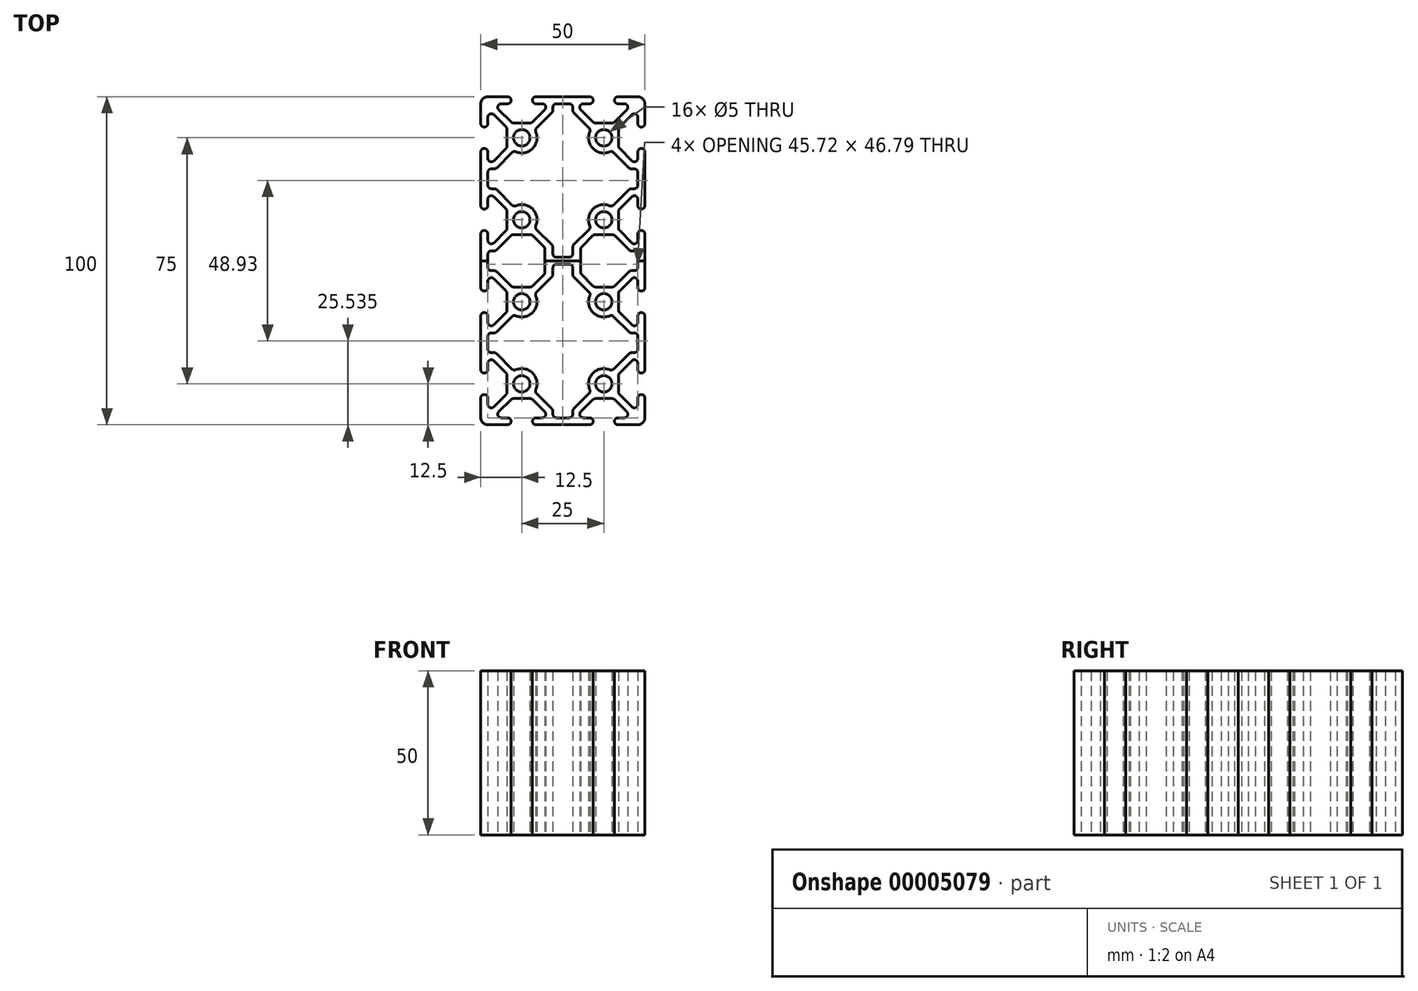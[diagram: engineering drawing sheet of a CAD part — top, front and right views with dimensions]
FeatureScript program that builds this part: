
annotation { "Feature Type Name" : "Feature", "Feature Type Description" : "" }
export const myFeature = defineFeature(function(context is Context, id is Id, definition is map)
    precondition{}
    {
        {
            var Q0;
            Q0=qCreatedBy(makeId("Top.planeOp"),FACE);
            var sketch = newSketch(context, id + "F0", { "sketchPlane" : qUnion([Q0])});
            skLineSegment(sketch, "E0", {"start": v(-12.5, 12.5) * mm, "end": v(-25, 25) * mm, "construction": true});
            skLineSegment(sketch, "E1", {"start": v(-25, 22.86) * mm, "end": v(-25, 16.82) * mm});
            skLineSegment(sketch, "E2", {"start": v(-22.86, 25) * mm, "end": v(-16.82, 25) * mm});
            skLineSegment(sketch, "E3", {"start": v(-16.82, 22.86) * mm, "end": v(-18.76, 22.86) * mm});
            skLineSegment(sketch, "E4", {"start": v(-22.86, 18.76) * mm, "end": v(-22.86, 16.82) * mm});
            skArc(sketch, "E5", {"start": v(-16.82, 25) * mm, "mid": v(-15.75, 23.93) * mm, "end": v(-16.82, 22.86) * mm});
            skArc(sketch, "E6", {"start": v(-22.86, 16.82) * mm, "mid": v(-23.93, 15.75) * mm, "end": v(-25, 16.82) * mm});
            skLineSegment(sketch, "E7", {"start": v(-19.52, 21.03) * mm, "end": v(-15.81, 17.32) * mm});
            skPoint(sketch, "E8.visualSharp", {"position": v(-25, 25) * mm});
            skLineSegment(sketch, "E8.filletArc", {"start": v(-25, 25) * mm, "end": v(-25, 25) * mm});
            skArc(sketch, "E9.filletArc", {"start": v(-21.03, 19.52) * mm, "mid": v(-22.2, 19.75) * mm, "end": v(-22.86, 18.76) * mm});
            skPoint(sketch, "E10.visualSharp", {"position": v(-21.35, 22.86) * mm});
            skArc(sketch, "E10.filletArc", {"start": v(-18.76, 22.86) * mm, "mid": v(-19.75, 22.2) * mm, "end": v(-19.52, 21.03) * mm});
            skArc(sketch, "E11.filletArc", {"start": v(-15.81, 17.32) * mm, "mid": v(-15.46, 17.1) * mm, "end": v(-15.05, 17.01) * mm});
            skCircle(sketch, "E12", {"center": v(-12.5, 12.5) * mm, "radius": 2.5 * mm});
            skLineSegment(sketch, "E13", {"start": v(0, 0) * mm, "end": v(0, 12.39) * mm, "construction": true});
            skCircle(sketch, "E14.0.MirrorC", {"center": v(12.5, 12.5) * mm, "radius": 2.5 * mm});
            skLineSegment(sketch, "E15", {"start": v(-12.5, 0) * mm, "end": v(-12.5, 12.5) * mm, "construction": true});
            skArc(sketch, "E16.0.MirrorCS", {"start": v(-9.19, 17.32) * mm, "mid": v(-9.54, 17.1) * mm, "end": v(-9.95, 17.01) * mm});
            skLineSegment(sketch, "E16.1.MirrorCS", {"start": v(-8.18, 22.86) * mm, "end": v(-6.24, 22.86) * mm});
            skLineSegment(sketch, "E16.3.MirrorCS", {"start": v(-5.48, 21.03) * mm, "end": v(-9.19, 17.32) * mm});
            skArc(sketch, "E16.8.MirrorCS", {"start": v(-8.18, 25) * mm, "mid": v(-9.25, 23.93) * mm, "end": v(-8.18, 22.86) * mm});
            skArc(sketch, "E16.11.MirrorCS", {"start": v(-6.24, 22.86) * mm, "mid": v(-5.25, 22.2) * mm, "end": v(-5.48, 21.03) * mm});
            skLineSegment(sketch, "E16.17.MirrorCS", {"start": v(0, 25) * mm, "end": v(-8.18, 25) * mm});
            skLineSegment(sketch, "E17", {"start": v(-15.05, 17.01) * mm, "end": v(-9.95, 17.01) * mm});
            skArc(sketch, "E18.1.MirrorCS", {"start": v(15.81, 17.32) * mm, "mid": v(15.46, 17.1) * mm, "end": v(15.05, 17.01) * mm});
            skArc(sketch, "E18.2.MirrorCS", {"start": v(9.19, 17.32) * mm, "mid": v(9.54, 17.1) * mm, "end": v(9.95, 17.01) * mm});
            skArc(sketch, "E18.3.MirrorCS", {"start": v(22.86, 16.82) * mm, "mid": v(23.93, 15.75) * mm, "end": v(25, 16.82) * mm});
            skLineSegment(sketch, "E18.5.MirrorCS", {"start": v(8.18, 22.86) * mm, "end": v(6.24, 22.86) * mm});
            skLineSegment(sketch, "E18.6.MirrorCS", {"start": v(19.52, 21.03) * mm, "end": v(15.81, 17.32) * mm});
            skLineSegment(sketch, "E18.7.MirrorCS", {"start": v(5.48, 21.03) * mm, "end": v(9.19, 17.32) * mm});
            skLineSegment(sketch, "E18.8.MirrorCS", {"start": v(12.5, 12.5) * mm, "end": v(25, 25) * mm, "construction": true});
            skArc(sketch, "E18.10.MirrorCS", {"start": v(16.82, 25) * mm, "mid": v(15.75, 23.93) * mm, "end": v(16.82, 22.86) * mm});
            skLineSegment(sketch, "E18.11.MirrorCS", {"start": v(15.05, 17.01) * mm, "end": v(9.95, 17.01) * mm});
            skPoint(sketch, "E18.12.MirrorP", {"position": v(21.35, 22.86) * mm});
            skLineSegment(sketch, "E18.14.MirrorCS", {"start": v(22.86, 25) * mm, "end": v(16.82, 25) * mm});
            skArc(sketch, "E18.15.MirrorCS", {"start": v(21.03, 19.52) * mm, "mid": v(22.2, 19.75) * mm, "end": v(22.86, 18.76) * mm});
            skPoint(sketch, "E18.16.MirrorP", {"position": v(25, 25) * mm});
            skLineSegment(sketch, "E18.17.MirrorCS", {"start": v(25, 22.86) * mm, "end": v(25, 16.82) * mm});
            skArc(sketch, "E18.18.MirrorCS", {"start": v(6.24, 22.86) * mm, "mid": v(5.25, 22.2) * mm, "end": v(5.48, 21.03) * mm});
            skArc(sketch, "E18.20.MirrorCS", {"start": v(18.76, 22.86) * mm, "mid": v(19.75, 22.2) * mm, "end": v(19.52, 21.03) * mm});
            skArc(sketch, "E18.21.MirrorCS", {"start": v(8.18, 25) * mm, "mid": v(9.25, 23.93) * mm, "end": v(8.18, 22.86) * mm});
            skLineSegment(sketch, "E18.22.MirrorCS", {"start": v(25, 25) * mm, "end": v(25, 25) * mm});
            skLineSegment(sketch, "E18.24.MirrorCS", {"start": v(22.86, 18.76) * mm, "end": v(22.86, 16.82) * mm});
            skLineSegment(sketch, "E18.25.MirrorCS", {"start": v(16.82, 22.86) * mm, "end": v(18.76, 22.86) * mm});
            skLineSegment(sketch, "E18.26.MirrorCS", {"start": v(0, 25) * mm, "end": v(8.18, 25) * mm});
            skLineSegment(sketch, "E19", {"start": v(-21.03, 19.52) * mm, "end": v(-17.32, 15.81) * mm});
            skLineSegment(sketch, "E20", {"start": v(0, 0) * mm, "end": v(-29.45, 0) * mm, "construction": true});
            skLineSegment(sketch, "E21", {"start": v(-17, 15.05) * mm, "end": v(-17, 12.5) * mm});
            skLineSegment(sketch, "E22", {"start": v(-12.5, 12.5) * mm, "end": v(-25, 12.5) * mm, "construction": true});
            skLineSegment(sketch, "E23.0.MirrorCS", {"start": v(21.03, 19.52) * mm, "end": v(17.32, 15.81) * mm});
            skLineSegment(sketch, "E24.0.MirrorCS", {"start": v(17, 15.05) * mm, "end": v(17, 12.5) * mm});
            skLineSegment(sketch, "E25.0.MirrorCS", {"start": v(-17, 9.95) * mm, "end": v(-17, 12.5) * mm});
            skLineSegment(sketch, "E26.0.MirrorCS", {"start": v(-21.03, 5.48) * mm, "end": v(-17.32, 9.19) * mm});
            skArc(sketch, "E27.0.MirrorCS", {"start": v(-21.03, 5.48) * mm, "mid": v(-22.2, 5.25) * mm, "end": v(-22.86, 6.24) * mm});
            skLineSegment(sketch, "E28.0.MirrorCS", {"start": v(-22.86, 6.24) * mm, "end": v(-22.86, 8.18) * mm});
            skArc(sketch, "E29.0.MirrorCS", {"start": v(-22.86, 8.18) * mm, "mid": v(-23.93, 9.25) * mm, "end": v(-25, 8.18) * mm});
            skLineSegment(sketch, "E30.0.MirrorCS", {"start": v(-25, 0) * mm, "end": v(-25, 8.18) * mm});
            skLineSegment(sketch, "E31.0.MirrorCS", {"start": v(17, 9.95) * mm, "end": v(17, 12.5) * mm});
            skLineSegment(sketch, "E32.0.MirrorCS", {"start": v(21.03, 5.48) * mm, "end": v(17.32, 9.19) * mm});
            skArc(sketch, "E33.0.MirrorCS", {"start": v(21.03, 5.48) * mm, "mid": v(22.2, 5.25) * mm, "end": v(22.86, 6.24) * mm});
            skLineSegment(sketch, "E34.0.MirrorCS", {"start": v(22.86, 6.24) * mm, "end": v(22.86, 8.18) * mm});
            skArc(sketch, "E35.0.MirrorCS", {"start": v(22.86, 8.18) * mm, "mid": v(23.93, 9.25) * mm, "end": v(25, 8.18) * mm});
            skLineSegment(sketch, "E36.0.MirrorCS", {"start": v(25, 0) * mm, "end": v(25, 8.18) * mm});
            skPoint(sketch, "E37.visualSharp", {"position": v(-17, 15.5) * mm});
            skArc(sketch, "E37.filletArc", {"start": v(-17, 15.05) * mm, "mid": v(-17.1, 15.46) * mm, "end": v(-17.32, 15.81) * mm});
            skPoint(sketch, "E38.visualSharp", {"position": v(-17, 9.5) * mm});
            skArc(sketch, "E38.filletArc", {"start": v(-17.32, 9.19) * mm, "mid": v(-17.1, 9.54) * mm, "end": v(-17, 9.95) * mm});
            skPoint(sketch, "E39.visualSharp", {"position": v(17, 9.5) * mm});
            skArc(sketch, "E39.filletArc", {"start": v(17, 9.95) * mm, "mid": v(17.1, 9.54) * mm, "end": v(17.32, 9.19) * mm});
            skPoint(sketch, "E40.visualSharp", {"position": v(17, 15.5) * mm});
            skArc(sketch, "E40.filletArc", {"start": v(17.32, 15.81) * mm, "mid": v(17.1, 15.46) * mm, "end": v(17, 15.05) * mm});
            skArc(sketch, "E41.1.MirrorCS", {"start": v(-17.32, -9.19) * mm, "mid": v(-17.1, -9.54) * mm, "end": v(-17, -9.95) * mm});
            skLineSegment(sketch, "E41.5.MirrorCS", {"start": v(-22.86, -6.24) * mm, "end": v(-22.86, -8.18) * mm});
            skLineSegment(sketch, "E41.8.MirrorCS", {"start": v(-12.5, 0) * mm, "end": v(-12.5, -12.5) * mm, "construction": true});
            skCircle(sketch, "E41.10.MirrorC", {"center": v(-12.5, -12.5) * mm, "radius": 2.5 * mm});
            skArc(sketch, "E41.12.MirrorCS", {"start": v(-21.03, -5.48) * mm, "mid": v(-22.2, -5.25) * mm, "end": v(-22.86, -6.24) * mm});
            skPoint(sketch, "E41.14.MirrorP", {"position": v(-17, -9.5) * mm});
            skLineSegment(sketch, "E41.15.MirrorCS", {"start": v(-21.03, -5.48) * mm, "end": v(-17.32, -9.19) * mm});
            skLineSegment(sketch, "E41.18.MirrorCS", {"start": v(-25, 0) * mm, "end": v(-25, -8.18) * mm});
            skArc(sketch, "E41.24.MirrorCS", {"start": v(-22.86, -8.18) * mm, "mid": v(-23.93, -9.25) * mm, "end": v(-25, -8.18) * mm});
            skLineSegment(sketch, "E41.29.MirrorCS", {"start": v(-12.5, -12.5) * mm, "end": v(-25, -12.5) * mm, "construction": true});
            skLineSegment(sketch, "E41.30.MirrorCS", {"start": v(-17, -9.95) * mm, "end": v(-17, -12.5) * mm});
            skArc(sketch, "E42.1.MirrorCS", {"start": v(17, -9.95) * mm, "mid": v(17.1, -9.54) * mm, "end": v(17.32, -9.19) * mm});
            skLineSegment(sketch, "E42.3.MirrorCS", {"start": v(22.86, -6.24) * mm, "end": v(22.86, -8.18) * mm});
            skArc(sketch, "E42.10.MirrorCS", {"start": v(21.03, -5.48) * mm, "mid": v(22.2, -5.25) * mm, "end": v(22.86, -6.24) * mm});
            skLineSegment(sketch, "E42.16.MirrorCS", {"start": v(17, -9.95) * mm, "end": v(17, -12.5) * mm});
            skArc(sketch, "E42.22.MirrorCS", {"start": v(22.86, -8.18) * mm, "mid": v(23.93, -9.25) * mm, "end": v(25, -8.18) * mm});
            skPoint(sketch, "E42.24.MirrorP", {"position": v(17, -9.5) * mm});
            skLineSegment(sketch, "E42.25.MirrorCS", {"start": v(21.03, -5.48) * mm, "end": v(17.32, -9.19) * mm});
            skCircle(sketch, "E42.27.MirrorC", {"center": v(12.5, -12.5) * mm, "radius": 2.5 * mm});
            skLineSegment(sketch, "E42.30.MirrorCS", {"start": v(25, 0) * mm, "end": v(25, -8.18) * mm});
            skArc(sketch, "E43.filletArc", {"start": v(-22.86, 25) * mm, "mid": v(-24.37, 24.37) * mm, "end": v(-25, 22.86) * mm});
            skArc(sketch, "E44.filletArc", {"start": v(25, 22.86) * mm, "mid": v(24.37, 24.37) * mm, "end": v(22.86, 25) * mm});
            skLineSegment(sketch, "E45", {"start": v(0, 22.86) * mm, "end": v(1.96, 22.86) * mm});
            skLineSegment(sketch, "E46", {"start": v(3.03, 21.8) * mm, "end": v(3.03, 20.9) * mm});
            skArc(sketch, "E47.0", {"start": v(14.31, 8.23) * mm, "mid": v(9.22, 9.22) * mm, "end": v(8.23, 14.31) * mm});
            skLineSegment(sketch, "E48.0", {"start": v(3.34, 20.15) * mm, "end": v(8, 15.49) * mm});
            skPoint(sketch, "E49.visualSharp", {"position": v(3.03, 22.86) * mm});
            skArc(sketch, "E49.filletArc", {"start": v(3.03, 21.8) * mm, "mid": v(2.71, 22.55) * mm, "end": v(1.96, 22.86) * mm});
            skPoint(sketch, "E50.visualSharp", {"position": v(8.55, 14.94) * mm});
            skArc(sketch, "E50.filletArc", {"start": v(8.23, 14.31) * mm, "mid": v(8.3, 14.93) * mm, "end": v(8, 15.49) * mm});
            skArc(sketch, "E51.0.MirrorCS", {"start": v(-14.31, 8.23) * mm, "mid": v(-9.22, 9.22) * mm, "end": v(-8.23, 14.31) * mm});
            skArc(sketch, "E52.0.MirrorCS", {"start": v(-8.23, 14.31) * mm, "mid": v(-8.3, 14.93) * mm, "end": v(-8, 15.49) * mm});
            skArc(sketch, "E53.0.MirrorCS", {"start": v(-3.03, 21.8) * mm, "mid": v(-2.71, 22.55) * mm, "end": v(-1.96, 22.86) * mm});
            skLineSegment(sketch, "E54.0.MirrorCS", {"start": v(0, 22.86) * mm, "end": v(-1.96, 22.86) * mm});
            skPoint(sketch, "E55.visualSharp", {"position": v(3.03, 20.46) * mm});
            skArc(sketch, "E55.filletArc", {"start": v(3.03, 20.9) * mm, "mid": v(3.1, 20.5) * mm, "end": v(3.34, 20.15) * mm});
            skLineSegment(sketch, "E56.0.MirrorCS", {"start": v(-3.34, 20.15) * mm, "end": v(-8, 15.49) * mm});
            skArc(sketch, "E57.0.MirrorCS", {"start": v(-3.03, 20.9) * mm, "mid": v(-3.1, 20.5) * mm, "end": v(-3.34, 20.15) * mm});
            skLineSegment(sketch, "E58.0.MirrorCS", {"start": v(-3.03, 21.8) * mm, "end": v(-3.03, 20.9) * mm});
            skPoint(sketch, "E59.visualSharp", {"position": v(-12.5, 7.86) * mm});
            skPoint(sketch, "E60.visualSharp", {"position": v(-12.5, -7.86) * mm});
            skPoint(sketch, "E61.visualSharp", {"position": v(12.5, -7.86) * mm});
            skArc(sketch, "E62.0.MirrorCS", {"start": v(-14.31, 8.23) * mm, "mid": v(-14.93, 8.3) * mm, "end": v(-15.49, 8) * mm});
            skLineSegment(sketch, "E63.0.MirrorCS", {"start": v(-20.15, 3.34) * mm, "end": v(-15.49, 8) * mm});
            skArc(sketch, "E64.0.MirrorCS", {"start": v(-20.9, 3.03) * mm, "mid": v(-20.5, 3.1) * mm, "end": v(-20.15, 3.34) * mm});
            skLineSegment(sketch, "E65.0.MirrorCS", {"start": v(-21.79, 3.03) * mm, "end": v(-20.9, 3.03) * mm});
            skArc(sketch, "E66.0.MirrorCS", {"start": v(-21.79, 3.03) * mm, "mid": v(-22.55, 2.71) * mm, "end": v(-22.86, 1.96) * mm});
            skLineSegment(sketch, "E67.0.MirrorCS", {"start": v(-22.86, 0) * mm, "end": v(-22.86, 1.96) * mm});
            skArc(sketch, "E68.0.MirrorCS", {"start": v(14.31, 8.23) * mm, "mid": v(14.93, 8.3) * mm, "end": v(15.49, 8) * mm});
            skArc(sketch, "E69.0.MirrorCS", {"start": v(-12.5, 7.86) * mm, "mid": v(-8.63, 9.94) * mm, "end": v(-8.23, 14.31) * mm});
            skLineSegment(sketch, "E70.0.MirrorCS", {"start": v(20.15, 3.34) * mm, "end": v(15.49, 8) * mm});
            skArc(sketch, "E71.0.MirrorCS", {"start": v(20.9, 3.03) * mm, "mid": v(20.5, 3.1) * mm, "end": v(20.15, 3.34) * mm});
            skLineSegment(sketch, "E72.0.MirrorCS", {"start": v(21.79, 3.03) * mm, "end": v(20.9, 3.03) * mm});
            skArc(sketch, "E73.0.MirrorCS", {"start": v(21.79, 3.03) * mm, "mid": v(22.55, 2.71) * mm, "end": v(22.86, 1.96) * mm});
            skLineSegment(sketch, "E74.0.MirrorCS", {"start": v(22.86, 0) * mm, "end": v(22.86, 1.96) * mm});
            skPoint(sketch, "E75.orphan", {"position": v(12.5, 7.86) * mm});
            skArc(sketch, "E76.0.MirrorCS", {"start": v(-20.9, -3.03) * mm, "mid": v(-20.5, -3.1) * mm, "end": v(-20.15, -3.34) * mm});
            skLineSegment(sketch, "E76.1.MirrorCS", {"start": v(-21.79, -3.03) * mm, "end": v(-20.9, -3.03) * mm});
            skArc(sketch, "E76.2.MirrorCS", {"start": v(-21.79, -3.03) * mm, "mid": v(-22.55, -2.71) * mm, "end": v(-22.86, -1.96) * mm});
            skLineSegment(sketch, "E76.3.MirrorCS", {"start": v(-22.86, 0) * mm, "end": v(-22.86, -1.96) * mm});
            skLineSegment(sketch, "E77.0.MirrorCS", {"start": v(-20.15, -3.34) * mm, "end": v(-15.49, -8) * mm});
            skArc(sketch, "E78.0.MirrorCS", {"start": v(-14.31, -8.23) * mm, "mid": v(-14.93, -8.3) * mm, "end": v(-15.49, -8) * mm});
            skArc(sketch, "E79.0.MirrorCS", {"start": v(-14.31, -8.23) * mm, "mid": v(-9.22, -9.22) * mm, "end": v(-8.23, -14.31) * mm});
            skArc(sketch, "E80.0.MirrorCS", {"start": v(14.31, -8.23) * mm, "mid": v(9.22, -9.22) * mm, "end": v(8.23, -14.31) * mm});
            skArc(sketch, "E81.0.MirrorCS", {"start": v(14.31, -8.23) * mm, "mid": v(14.93, -8.3) * mm, "end": v(15.49, -8) * mm});
            skLineSegment(sketch, "E82.0.MirrorCS", {"start": v(20.15, -3.34) * mm, "end": v(15.49, -8) * mm});
            skArc(sketch, "E83.0.MirrorCS", {"start": v(20.9, -3.03) * mm, "mid": v(20.5, -3.1) * mm, "end": v(20.15, -3.34) * mm});
            skLineSegment(sketch, "E84.0.MirrorCS", {"start": v(21.79, -3.03) * mm, "end": v(20.9, -3.03) * mm});
            skArc(sketch, "E85.0.MirrorCS", {"start": v(21.79, -3.03) * mm, "mid": v(22.55, -2.71) * mm, "end": v(22.86, -1.96) * mm});
            skLineSegment(sketch, "E86.0.MirrorCS", {"start": v(22.86, 0) * mm, "end": v(22.86, -1.96) * mm});
            skArc(sketch, "E87.1.MirrorCS", {"start": v(14.31, -33.23) * mm, "mid": v(14.93, -33.3) * mm, "end": v(15.49, -33) * mm});
            skLineSegment(sketch, "E87.2.MirrorCS", {"start": v(22.86, -25) * mm, "end": v(22.86, -23.04) * mm});
            skLineSegment(sketch, "E87.3.MirrorCS", {"start": v(21.79, -28.03) * mm, "end": v(20.9, -28.03) * mm});
            skLineSegment(sketch, "E87.4.MirrorCS", {"start": v(-22.86, -25) * mm, "end": v(-22.86, -23.04) * mm});
            skArc(sketch, "E87.5.MirrorCS", {"start": v(20.9, -28.03) * mm, "mid": v(20.5, -28.1) * mm, "end": v(20.15, -28.34) * mm});
            skArc(sketch, "E87.6.MirrorCS", {"start": v(21.79, -21.97) * mm, "mid": v(22.55, -22.29) * mm, "end": v(22.86, -23.04) * mm});
            skArc(sketch, "E87.7.MirrorCS", {"start": v(-21.79, -28.03) * mm, "mid": v(-22.55, -27.71) * mm, "end": v(-22.86, -26.96) * mm});
            skLineSegment(sketch, "E87.8.MirrorCS", {"start": v(-22.86, -18.76) * mm, "end": v(-22.86, -16.82) * mm});
            skArc(sketch, "E87.10.MirrorCS", {"start": v(-21.79, -21.97) * mm, "mid": v(-22.55, -22.29) * mm, "end": v(-22.86, -23.04) * mm});
            skLineSegment(sketch, "E87.12.MirrorCS", {"start": v(-21.79, -28.03) * mm, "end": v(-20.9, -28.03) * mm});
            skLineSegment(sketch, "E87.14.MirrorCS", {"start": v(-22.86, -31.24) * mm, "end": v(-22.86, -33.18) * mm});
            skArc(sketch, "E87.15.MirrorCS", {"start": v(17, -15.05) * mm, "mid": v(17.1, -15.46) * mm, "end": v(17.32, -15.81) * mm});
            skArc(sketch, "E87.16.MirrorCS", {"start": v(17, -34.95) * mm, "mid": v(17.1, -34.54) * mm, "end": v(17.32, -34.19) * mm});
            skLineSegment(sketch, "E87.17.MirrorCS", {"start": v(22.86, -25) * mm, "end": v(22.86, -26.96) * mm});
            skArc(sketch, "E87.18.MirrorCS", {"start": v(-20.9, -28.03) * mm, "mid": v(-20.5, -28.1) * mm, "end": v(-20.15, -28.34) * mm});
            skLineSegment(sketch, "E87.19.MirrorCS", {"start": v(22.86, -18.76) * mm, "end": v(22.86, -16.82) * mm});
            skArc(sketch, "E87.20.MirrorCS", {"start": v(20.9, -21.97) * mm, "mid": v(20.5, -21.9) * mm, "end": v(20.15, -21.66) * mm});
            skArc(sketch, "E87.21.MirrorCS", {"start": v(-17.32, -34.19) * mm, "mid": v(-17.1, -34.54) * mm, "end": v(-17.01, -34.95) * mm});
            skLineSegment(sketch, "E87.22.MirrorCS", {"start": v(22.86, -31.24) * mm, "end": v(22.86, -33.18) * mm});
            skLineSegment(sketch, "E87.23.MirrorCS", {"start": v(-22.86, -25) * mm, "end": v(-22.86, -26.96) * mm});
            skArc(sketch, "E87.24.MirrorCS", {"start": v(-20.9, -21.97) * mm, "mid": v(-20.5, -21.9) * mm, "end": v(-20.15, -21.66) * mm});
            skLineSegment(sketch, "E87.25.MirrorCS", {"start": v(21.79, -21.97) * mm, "end": v(20.9, -21.97) * mm});
            skLineSegment(sketch, "E87.26.MirrorCS", {"start": v(-21.79, -21.97) * mm, "end": v(-20.9, -21.97) * mm});
            skArc(sketch, "E87.27.MirrorCS", {"start": v(21.79, -28.03) * mm, "mid": v(22.55, -27.71) * mm, "end": v(22.86, -26.96) * mm});
            skArc(sketch, "E87.28.MirrorCS", {"start": v(-17.32, -15.81) * mm, "mid": v(-17.1, -15.46) * mm, "end": v(-17, -15.05) * mm});
            skLineSegment(sketch, "E87.29.MirrorCS", {"start": v(-25, -25) * mm, "end": v(-25, -33.18) * mm});
            skLineSegment(sketch, "E87.30.MirrorCS", {"start": v(17.01, -9.95) * mm, "end": v(17.01, -12.5) * mm});
            skLineSegment(sketch, "E87.31.MirrorCS", {"start": v(21.03, -19.52) * mm, "end": v(17.32, -15.81) * mm});
            skLineSegment(sketch, "E87.32.MirrorCS", {"start": v(-20.15, -28.34) * mm, "end": v(-15.81, -32.68) * mm});
            skPoint(sketch, "E87.33.MirrorP", {"position": v(-17, -15.5) * mm});
            skArc(sketch, "E87.35.MirrorCS", {"start": v(-22.86, -16.82) * mm, "mid": v(-23.93, -15.75) * mm, "end": v(-25, -16.82) * mm});
            skLineSegment(sketch, "E87.36.MirrorCS", {"start": v(-21.03, -30.48) * mm, "end": v(-17.32, -34.19) * mm});
            skLineSegment(sketch, "E87.37.MirrorCS", {"start": v(20.15, -21.66) * mm, "end": v(15.81, -17.32) * mm});
            skArc(sketch, "E87.38.MirrorCS", {"start": v(-21.03, -19.52) * mm, "mid": v(-22.2, -19.75) * mm, "end": v(-22.86, -18.76) * mm});
            skArc(sketch, "E87.39.MirrorCS", {"start": v(-22.86, -33.18) * mm, "mid": v(-23.93, -34.25) * mm, "end": v(-25, -33.18) * mm});
            skLineSegment(sketch, "E87.41.MirrorCS", {"start": v(0, -25) * mm, "end": v(-29.45, -25) * mm, "construction": true});
            skLineSegment(sketch, "E87.42.MirrorCS", {"start": v(-17, -15.05) * mm, "end": v(-17, -12.5) * mm});
            skArc(sketch, "E87.43.MirrorCS", {"start": v(22.86, -33.18) * mm, "mid": v(23.93, -34.25) * mm, "end": v(25, -33.18) * mm});
            skLineSegment(sketch, "E87.44.MirrorCS", {"start": v(17, -15.05) * mm, "end": v(17, -12.5) * mm});
            skLineSegment(sketch, "E87.46.MirrorCS", {"start": v(21.03, -30.48) * mm, "end": v(17.32, -34.19) * mm});
            skPoint(sketch, "E87.48.MirrorP", {"position": v(17, -15.5) * mm});
            skPoint(sketch, "E87.49.MirrorP", {"position": v(-17.01, -34.5) * mm});
            skPoint(sketch, "E87.50.MirrorP", {"position": v(-12.5, -17.14) * mm});
            skLineSegment(sketch, "E87.51.MirrorCS", {"start": v(25, -25) * mm, "end": v(25, -33.18) * mm});
            skLineSegment(sketch, "E87.52.MirrorCS", {"start": v(25, -25) * mm, "end": v(25, -16.82) * mm});
            skLineSegment(sketch, "E87.53.MirrorCS", {"start": v(17, -34.95) * mm, "end": v(17, -37.5) * mm});
            skArc(sketch, "E87.54.MirrorCS", {"start": v(21.03, -30.48) * mm, "mid": v(22.2, -30.25) * mm, "end": v(22.86, -31.24) * mm});
            skLineSegment(sketch, "E87.55.MirrorCS", {"start": v(-25, -25) * mm, "end": v(-25, -16.82) * mm});
            skLineSegment(sketch, "E87.57.MirrorCS", {"start": v(-20.15, -21.66) * mm, "end": v(-15.81, -17.32) * mm});
            skPoint(sketch, "E87.58.MirrorP", {"position": v(12.5, -32.86) * mm});
            skPoint(sketch, "E87.59.MirrorP", {"position": v(17, -34.5) * mm});
            skLineSegment(sketch, "E87.60.MirrorCS", {"start": v(-12.5, -37.5) * mm, "end": v(-25, -37.5) * mm, "construction": true});
            skArc(sketch, "E87.61.MirrorCS", {"start": v(21.03, -19.52) * mm, "mid": v(22.2, -19.75) * mm, "end": v(22.86, -18.76) * mm});
            skLineSegment(sketch, "E87.62.MirrorCS", {"start": v(0, -25) * mm, "end": v(0, -37.39) * mm, "construction": true});
            skLineSegment(sketch, "E87.64.MirrorCS", {"start": v(20.15, -28.34) * mm, "end": v(15.81, -32.68) * mm});
            skArc(sketch, "E87.65.MirrorCS", {"start": v(22.86, -16.82) * mm, "mid": v(23.93, -15.75) * mm, "end": v(25, -16.82) * mm});
            skLineSegment(sketch, "E87.66.MirrorCS", {"start": v(-17.01, -34.95) * mm, "end": v(-17.01, -37.5) * mm});
            skLineSegment(sketch, "E87.67.MirrorCS", {"start": v(-12.5, -25) * mm, "end": v(-12.5, -37.5) * mm, "construction": true});
            skArc(sketch, "E87.68.MirrorCS", {"start": v(-21.03, -30.48) * mm, "mid": v(-22.2, -30.25) * mm, "end": v(-22.86, -31.24) * mm});
            skLineSegment(sketch, "E87.69.MirrorCS", {"start": v(-12.5, -25) * mm, "end": v(-12.5, -12.5) * mm, "construction": true});
            skLineSegment(sketch, "E87.70.MirrorCS", {"start": v(-21.03, -19.52) * mm, "end": v(-17.32, -15.81) * mm});
            skLineSegment(sketch, "E88.0.MirrorCS", {"start": v(-3.34, -20.15) * mm, "end": v(-8, -15.49) * mm});
            skLineSegment(sketch, "E89.0.MirrorCS", {"start": v(-5.8, -20.72) * mm, "end": v(-9.19, -17.32) * mm});
            skArc(sketch, "E90.0.MirrorCS", {"start": v(-3.03, -20.9) * mm, "mid": v(-3.1, -20.5) * mm, "end": v(-3.34, -20.15) * mm});
            skLineSegment(sketch, "E91.0.MirrorCS", {"start": v(-3.03, -22.86) * mm, "end": v(-3.03, -20.9) * mm});
            skLineSegment(sketch, "E92.0.MirrorCS", {"start": v(3.34, -20.15) * mm, "end": v(8, -15.49) * mm});
            skArc(sketch, "E93.0.MirrorCS", {"start": v(3.03, -20.9) * mm, "mid": v(3.1, -20.5) * mm, "end": v(3.34, -20.15) * mm});
            skLineSegment(sketch, "E94.0.MirrorCS", {"start": v(3.03, -22.86) * mm, "end": v(3.03, -20.9) * mm});
            skPoint(sketch, "E95.newPointA", {"position": v(-8.23, -14.31) * mm});
            skPoint(sketch, "E95.newPointB", {"position": v(-8, -15.49) * mm});
            skArc(sketch, "E95.filletArc", {"start": v(-8.23, -14.31) * mm, "mid": v(-8.3, -14.93) * mm, "end": v(-8, -15.49) * mm});
            skPoint(sketch, "E96.newPointA", {"position": v(8.23, -14.31) * mm});
            skPoint(sketch, "E96.newPointB", {"position": v(8, -15.49) * mm});
            skArc(sketch, "E96.filletArc", {"start": v(8, -15.49) * mm, "mid": v(8.3, -14.93) * mm, "end": v(8.23, -14.31) * mm});
            skLineSegment(sketch, "E97.0.MirrorCS", {"start": v(-15.05, -17.01) * mm, "end": v(-9.95, -17.01) * mm});
            skPoint(sketch, "E98.newPointB", {"position": v(-15.05, -17.01) * mm});
            skArc(sketch, "E98.filletArc", {"start": v(-15.05, -17.01) * mm, "mid": v(-15.46, -17.1) * mm, "end": v(-15.81, -17.32) * mm});
            skPoint(sketch, "E99.visualSharp", {"position": v(-9.5, -17) * mm});
            skArc(sketch, "E99.filletArc", {"start": v(-9.19, -17.32) * mm, "mid": v(-9.54, -17.1) * mm, "end": v(-9.95, -17.01) * mm});
            skLineSegment(sketch, "E100.0.MirrorCS", {"start": v(-15.05, -32.99) * mm, "end": v(-9.95, -32.99) * mm});
            skLineSegment(sketch, "E101.0.MirrorCS", {"start": v(-5.8, -29.28) * mm, "end": v(-9.19, -32.68) * mm});
            skPoint(sketch, "E102.newPointB", {"position": v(-15.05, -32.99) * mm});
            skArc(sketch, "E102.filletArc", {"start": v(-15.81, -32.68) * mm, "mid": v(-15.46, -32.9) * mm, "end": v(-15.05, -32.99) * mm});
            skPoint(sketch, "E103.newPointA", {"position": v(-9.19, -32.68) * mm});
            skPoint(sketch, "E103.newPointB", {"position": v(-9.95, -32.99) * mm});
            skArc(sketch, "E103.filletArc", {"start": v(-9.95, -32.99) * mm, "mid": v(-9.54, -32.9) * mm, "end": v(-9.19, -32.68) * mm});
            skLineSegment(sketch, "E104", {"start": v(-5.48, -21.48) * mm, "end": v(-5.48, -28.52) * mm});
            skPoint(sketch, "E105.visualSharp", {"position": v(-5.48, -21.03) * mm});
            skArc(sketch, "E105.filletArc", {"start": v(-5.48, -21.48) * mm, "mid": v(-5.56, -21.07) * mm, "end": v(-5.8, -20.72) * mm});
            skPoint(sketch, "E106.visualSharp", {"position": v(-5.48, -28.97) * mm});
            skArc(sketch, "E106.filletArc", {"start": v(-5.8, -29.28) * mm, "mid": v(-5.56, -28.93) * mm, "end": v(-5.48, -28.52) * mm});
            skLineSegment(sketch, "E107", {"start": v(-1.96, -23.93) * mm, "end": v(1.96, -23.93) * mm});
            skPoint(sketch, "E108.orphan", {"position": v(-3.03, -21.8) * mm});
            skPoint(sketch, "E109.orphan", {"position": v(3.03, -21.8) * mm});
            skArc(sketch, "E110.filletArc", {"start": v(-3.03, -22.86) * mm, "mid": v(-2.71, -23.62) * mm, "end": v(-1.96, -23.93) * mm});
            skArc(sketch, "E111.filletArc", {"start": v(1.96, -23.93) * mm, "mid": v(2.71, -23.62) * mm, "end": v(3.03, -22.86) * mm});
            skLineSegment(sketch, "E112.0.MirrorCS", {"start": v(15.05, -17.01) * mm, "end": v(9.95, -17.01) * mm});
            skLineSegment(sketch, "E113.0.MirrorCS", {"start": v(5.8, -20.72) * mm, "end": v(9.19, -17.32) * mm});
            skLineSegment(sketch, "E114.0.MirrorCS", {"start": v(5.48, -21.48) * mm, "end": v(5.48, -28.52) * mm});
            skLineSegment(sketch, "E115.0.MirrorCS", {"start": v(5.8, -29.28) * mm, "end": v(9.19, -32.68) * mm});
            skLineSegment(sketch, "E116.0.MirrorCS", {"start": v(15.05, -33) * mm, "end": v(9.95, -33) * mm});
            skPoint(sketch, "E117.newPointA", {"position": v(9.19, -17.32) * mm});
            skPoint(sketch, "E117.newPointB", {"position": v(9.95, -17.01) * mm});
            skArc(sketch, "E117.filletArc", {"start": v(9.95, -17.01) * mm, "mid": v(9.54, -17.1) * mm, "end": v(9.19, -17.32) * mm});
            skPoint(sketch, "E118.newPointA", {"position": v(15.05, -17.01) * mm});
            skArc(sketch, "E118.filletArc", {"start": v(15.81, -17.32) * mm, "mid": v(15.46, -17.1) * mm, "end": v(15.05, -17.01) * mm});
            skPoint(sketch, "E119.newPointA", {"position": v(15.05, -33) * mm});
            skPoint(sketch, "E119.newPointB", {"position": v(15.49, -33) * mm});
            skArc(sketch, "E119.filletArc", {"start": v(15.05, -33) * mm, "mid": v(15.46, -32.9) * mm, "end": v(15.81, -32.68) * mm});
            skPoint(sketch, "E120.newPointA", {"position": v(5.8, -29.28) * mm});
            skPoint(sketch, "E120.newPointB", {"position": v(5.48, -28.52) * mm});
            skArc(sketch, "E120.filletArc", {"start": v(5.48, -28.52) * mm, "mid": v(5.56, -28.93) * mm, "end": v(5.8, -29.28) * mm});
            skPoint(sketch, "E121.newPointA", {"position": v(9.19, -32.68) * mm});
            skPoint(sketch, "E121.newPointB", {"position": v(9.95, -33) * mm});
            skArc(sketch, "E121.filletArc", {"start": v(9.19, -32.68) * mm, "mid": v(9.54, -32.9) * mm, "end": v(9.95, -33) * mm});
            skPoint(sketch, "E122.newPointA", {"position": v(5.8, -20.72) * mm});
            skPoint(sketch, "E122.newPointB", {"position": v(5.48, -21.48) * mm});
            skArc(sketch, "E122.filletArc", {"start": v(5.8, -20.72) * mm, "mid": v(5.56, -21.07) * mm, "end": v(5.48, -21.48) * mm});
            skLineSegment(sketch, "E123.0.MirrorCS", {"start": v(-17.01, -40.05) * mm, "end": v(-17.01, -37.5) * mm});
            skLineSegment(sketch, "E124", {"start": v(-25, -25) * mm, "end": v(25, -25) * mm});
            skSolve(sketch);
        }
        {
            var Q0;
            Q0=makeQuery(id+"F0.imprint","IMPRINT",FACE,{"disambiguationData":[TD([[makeQuery(id+"F0.imprint","IMPRINT",EDGE,{"derivedFrom":sQuery(id+"F0.wireOp",EDGE,"E1")}),1.0]])]});
            extrude(context, id + "F1", {"entities" : qUnion([Q0]), "depth" : 50 * mm});
        }
        {
            var Q0;
            Q0=makeQuery(id+"F1.opExtrude","SWEPT_BODY",BODY,{"disambiguationData":[OSD([sQuery(id+"F0.wireOp",EDGE,"E1"),sQuery(id+"F0.wireOp",EDGE,"E2"),sQuery(id+"F0.wireOp",EDGE,"E3"),sQuery(id+"F0.wireOp",EDGE,"E4"),sQuery(id+"F0.wireOp",EDGE,"E5"),sQuery(id+"F0.wireOp",EDGE,"E6"),sQuery(id+"F0.wireOp",EDGE,"E7"),sQuery(id+"F0.wireOp",EDGE,"E9.filletArc"),sQuery(id+"F0.wireOp",EDGE,"E10.filletArc"),sQuery(id+"F0.wireOp",EDGE,"E11.filletArc"),sQuery(id+"F0.wireOp",EDGE,"E12"),sQuery(id+"F0.wireOp",EDGE,"E14.0.MirrorC"),sQuery(id+"F0.wireOp",EDGE,"E16.0.MirrorCS"),sQuery(id+"F0.wireOp",EDGE,"E16.1.MirrorCS"),sQuery(id+"F0.wireOp",EDGE,"E16.3.MirrorCS"),sQuery(id+"F0.wireOp",EDGE,"E16.8.MirrorCS"),sQuery(id+"F0.wireOp",EDGE,"E16.11.MirrorCS"),sQuery(id+"F0.wireOp",EDGE,"E17"),sQuery(id+"F0.wireOp",EDGE,"E18.1.MirrorCS"),sQuery(id+"F0.wireOp",EDGE,"E18.2.MirrorCS"),sQuery(id+"F0.wireOp",EDGE,"E18.5.MirrorCS"),sQuery(id+"F0.wireOp",EDGE,"E18.6.MirrorCS"),sQuery(id+"F0.wireOp",EDGE,"E18.7.MirrorCS"),sQuery(id+"F0.wireOp",EDGE,"E18.10.MirrorCS"),sQuery(id+"F0.wireOp",EDGE,"E18.11.MirrorCS"),sQuery(id+"F0.wireOp",EDGE,"E18.14.MirrorCS"),sQuery(id+"F0.wireOp",EDGE,"E18.15.MirrorCS"),sQuery(id+"F0.wireOp",EDGE,"E18.17.MirrorCS"),sQuery(id+"F0.wireOp",EDGE,"E18.18.MirrorCS"),sQuery(id+"F0.wireOp",EDGE,"E18.20.MirrorCS"),sQuery(id+"F0.wireOp",EDGE,"E18.21.MirrorCS"),sQuery(id+"F0.wireOp",EDGE,"E18.24.MirrorCS"),sQuery(id+"F0.wireOp",EDGE,"E18.25.MirrorCS"),sQuery(id+"F0.wireOp",EDGE,"E18.26.MirrorCS"),sQuery(id+"F0.wireOp",EDGE,"E18.3.MirrorCS"),sQuery(id+"F0.wireOp",EDGE,"E19"),sQuery(id+"F0.wireOp",EDGE,"E21"),sQuery(id+"F0.wireOp",EDGE,"E23.0.MirrorCS"),sQuery(id+"F0.wireOp",EDGE,"E26.0.MirrorCS"),sQuery(id+"F0.wireOp",EDGE,"E27.0.MirrorCS"),sQuery(id+"F0.wireOp",EDGE,"E28.0.MirrorCS"),sQuery(id+"F0.wireOp",EDGE,"E29.0.MirrorCS"),sQuery(id+"F0.wireOp",EDGE,"E30.0.MirrorCS"),sQuery(id+"F0.wireOp",EDGE,"E31.0.MirrorCS"),sQuery(id+"F0.wireOp",EDGE,"E32.0.MirrorCS"),sQuery(id+"F0.wireOp",EDGE,"E33.0.MirrorCS"),sQuery(id+"F0.wireOp",EDGE,"E34.0.MirrorCS"),sQuery(id+"F0.wireOp",EDGE,"E35.0.MirrorCS"),sQuery(id+"F0.wireOp",EDGE,"E37.filletArc"),sQuery(id+"F0.wireOp",EDGE,"E38.filletArc"),sQuery(id+"F0.wireOp",EDGE,"E39.filletArc"),sQuery(id+"F0.wireOp",EDGE,"E40.filletArc"),sQuery(id+"F0.wireOp",EDGE,"E41.1.MirrorCS"),sQuery(id+"F0.wireOp",EDGE,"E41.5.MirrorCS"),sQuery(id+"F0.wireOp",EDGE,"E41.12.MirrorCS"),sQuery(id+"F0.wireOp",EDGE,"E41.15.MirrorCS"),sQuery(id+"F0.wireOp",EDGE,"E41.24.MirrorCS"),sQuery(id+"F0.wireOp",EDGE,"E42.1.MirrorCS"),sQuery(id+"F0.wireOp",EDGE,"E42.3.MirrorCS"),sQuery(id+"F0.wireOp",EDGE,"E42.10.MirrorCS"),sQuery(id+"F0.wireOp",EDGE,"E42.22.MirrorCS"),sQuery(id+"F0.wireOp",EDGE,"E42.25.MirrorCS"),sQuery(id+"F0.wireOp",EDGE,"E42.30.MirrorCS"),sQuery(id+"F0.wireOp",EDGE,"E43.filletArc"),sQuery(id+"F0.wireOp",EDGE,"E44.filletArc"),sQuery(id+"F0.wireOp",EDGE,"E45"),sQuery(id+"F0.wireOp",EDGE,"E46"),sQuery(id+"F0.wireOp",EDGE,"E47.0"),sQuery(id+"F0.wireOp",EDGE,"E48.0"),sQuery(id+"F0.wireOp",EDGE,"E49.filletArc"),sQuery(id+"F0.wireOp",EDGE,"E50.filletArc"),sQuery(id+"F0.wireOp",EDGE,"E51.0.MirrorCS"),sQuery(id+"F0.wireOp",EDGE,"E52.0.MirrorCS"),sQuery(id+"F0.wireOp",EDGE,"E53.0.MirrorCS"),sQuery(id+"F0.wireOp",EDGE,"E55.filletArc"),sQuery(id+"F0.wireOp",EDGE,"E56.0.MirrorCS"),sQuery(id+"F0.wireOp",EDGE,"E57.0.MirrorCS"),sQuery(id+"F0.wireOp",EDGE,"E58.0.MirrorCS"),sQuery(id+"F0.wireOp",EDGE,"E62.0.MirrorCS"),sQuery(id+"F0.wireOp",EDGE,"E63.0.MirrorCS"),sQuery(id+"F0.wireOp",EDGE,"E64.0.MirrorCS"),sQuery(id+"F0.wireOp",EDGE,"E65.0.MirrorCS"),sQuery(id+"F0.wireOp",EDGE,"E66.0.MirrorCS"),sQuery(id+"F0.wireOp",EDGE,"E67.0.MirrorCS"),sQuery(id+"F0.wireOp",EDGE,"E69.0.MirrorCS"),sQuery(id+"F0.wireOp",EDGE,"E68.0.MirrorCS"),sQuery(id+"F0.wireOp",EDGE,"E70.0.MirrorCS"),sQuery(id+"F0.wireOp",EDGE,"E71.0.MirrorCS"),sQuery(id+"F0.wireOp",EDGE,"E72.0.MirrorCS"),sQuery(id+"F0.wireOp",EDGE,"E73.0.MirrorCS"),sQuery(id+"F0.wireOp",EDGE,"E74.0.MirrorCS"),sQuery(id+"F0.wireOp",EDGE,"E76.0.MirrorCS"),sQuery(id+"F0.wireOp",EDGE,"E76.1.MirrorCS"),sQuery(id+"F0.wireOp",EDGE,"E76.2.MirrorCS"),sQuery(id+"F0.wireOp",EDGE,"E76.3.MirrorCS"),sQuery(id+"F0.wireOp",EDGE,"E77.0.MirrorCS"),sQuery(id+"F0.wireOp",EDGE,"E78.0.MirrorCS"),sQuery(id+"F0.wireOp",EDGE,"E79.0.MirrorCS"),sQuery(id+"F0.wireOp",EDGE,"E80.0.MirrorCS"),sQuery(id+"F0.wireOp",EDGE,"E81.0.MirrorCS"),sQuery(id+"F0.wireOp",EDGE,"E82.0.MirrorCS"),sQuery(id+"F0.wireOp",EDGE,"E83.0.MirrorCS"),sQuery(id+"F0.wireOp",EDGE,"E84.0.MirrorCS"),sQuery(id+"F0.wireOp",EDGE,"E85.0.MirrorCS"),sQuery(id+"F0.wireOp",EDGE,"E86.0.MirrorCS"),sQuery(id+"F0.wireOp",EDGE,"E87.2.MirrorCS"),sQuery(id+"F0.wireOp",EDGE,"E87.4.MirrorCS"),sQuery(id+"F0.wireOp",EDGE,"E87.6.MirrorCS"),sQuery(id+"F0.wireOp",EDGE,"E87.8.MirrorCS"),sQuery(id+"F0.wireOp",EDGE,"E87.10.MirrorCS"),sQuery(id+"F0.wireOp",EDGE,"E87.15.MirrorCS"),sQuery(id+"F0.wireOp",EDGE,"E87.19.MirrorCS"),sQuery(id+"F0.wireOp",EDGE,"E87.20.MirrorCS"),sQuery(id+"F0.wireOp",EDGE,"E87.24.MirrorCS"),sQuery(id+"F0.wireOp",EDGE,"E87.25.MirrorCS"),sQuery(id+"F0.wireOp",EDGE,"E87.26.MirrorCS"),sQuery(id+"F0.wireOp",EDGE,"E87.28.MirrorCS"),sQuery(id+"F0.wireOp",EDGE,"E87.31.MirrorCS"),sQuery(id+"F0.wireOp",EDGE,"E87.35.MirrorCS"),sQuery(id+"F0.wireOp",EDGE,"E87.37.MirrorCS"),sQuery(id+"F0.wireOp",EDGE,"E87.38.MirrorCS"),sQuery(id+"F0.wireOp",EDGE,"E87.44.MirrorCS"),sQuery(id+"F0.wireOp",EDGE,"E41.30.MirrorCS"),sQuery(id+"F0.wireOp",EDGE,"E87.52.MirrorCS"),sQuery(id+"F0.wireOp",EDGE,"E87.55.MirrorCS"),sQuery(id+"F0.wireOp",EDGE,"E41.10.MirrorC"),sQuery(id+"F0.wireOp",EDGE,"E87.57.MirrorCS"),sQuery(id+"F0.wireOp",EDGE,"E87.61.MirrorCS"),sQuery(id+"F0.wireOp",EDGE,"E87.65.MirrorCS"),sQuery(id+"F0.wireOp",EDGE,"E87.70.MirrorCS"),sQuery(id+"F0.wireOp",EDGE,"E42.27.MirrorC"),sQuery(id+"F0.wireOp",EDGE,"E88.0.MirrorCS"),sQuery(id+"F0.wireOp",EDGE,"E89.0.MirrorCS"),sQuery(id+"F0.wireOp",EDGE,"E90.0.MirrorCS"),sQuery(id+"F0.wireOp",EDGE,"E91.0.MirrorCS"),sQuery(id+"F0.wireOp",EDGE,"E92.0.MirrorCS"),sQuery(id+"F0.wireOp",EDGE,"E93.0.MirrorCS"),sQuery(id+"F0.wireOp",EDGE,"E94.0.MirrorCS"),sQuery(id+"F0.wireOp",EDGE,"E95.filletArc"),sQuery(id+"F0.wireOp",EDGE,"E96.filletArc"),sQuery(id+"F0.wireOp",EDGE,"E97.0.MirrorCS"),sQuery(id+"F0.wireOp",EDGE,"E98.filletArc"),sQuery(id+"F0.wireOp",EDGE,"E99.filletArc"),sQuery(id+"F0.wireOp",EDGE,"E104"),sQuery(id+"F0.wireOp",EDGE,"E105.filletArc"),sQuery(id+"F0.wireOp",EDGE,"E54.0.MirrorCS"),sQuery(id+"F0.wireOp",EDGE,"E107"),sQuery(id+"F0.wireOp",EDGE,"E110.filletArc"),sQuery(id+"F0.wireOp",EDGE,"E111.filletArc"),sQuery(id+"F0.wireOp",EDGE,"E112.0.MirrorCS"),sQuery(id+"F0.wireOp",EDGE,"E113.0.MirrorCS"),sQuery(id+"F0.wireOp",EDGE,"E114.0.MirrorCS"),sQuery(id+"F0.wireOp",EDGE,"E117.filletArc"),sQuery(id+"F0.wireOp",EDGE,"E118.filletArc"),sQuery(id+"F0.wireOp",EDGE,"E122.filletArc"),sQuery(id+"F0.wireOp",EDGE,"E124")])]});
            var Q1;
            {var subQ0=sQuery(id+"F0.wireOp",EDGE,"E124");Q1=makeQuery(id+"F1.opExtrude","SWEPT_FACE",FACE,{"disambiguationData":[OSD([subQ0]),TDD([makeQuery(id+"F0.imprint","IMPRINT",EDGE,{"disambiguationData":[TD([[makeQuery(id+"F0.imprint","INTERSECT",VERTEX,{"derivedFrom":[sQuery(id+"F0.wireOp",EDGE,"E104"),subQ0]}),-1.0]])],"derivedFrom":subQ0})])]});}
            mirror(context, id + "F2", {"entities" : qUnion([Q0]), "mirrorPlane" : qUnion([Q1])});
        }
        {
            var Q0;
            Q0=makeQuery(id+"F1.opExtrude","SWEPT_BODY",BODY,{"disambiguationData":[OSD([sQuery(id+"F0.wireOp",EDGE,"E1"),sQuery(id+"F0.wireOp",EDGE,"E2"),sQuery(id+"F0.wireOp",EDGE,"E3"),sQuery(id+"F0.wireOp",EDGE,"E4"),sQuery(id+"F0.wireOp",EDGE,"E5"),sQuery(id+"F0.wireOp",EDGE,"E6"),sQuery(id+"F0.wireOp",EDGE,"E7"),sQuery(id+"F0.wireOp",EDGE,"E9.filletArc"),sQuery(id+"F0.wireOp",EDGE,"E10.filletArc"),sQuery(id+"F0.wireOp",EDGE,"E11.filletArc"),sQuery(id+"F0.wireOp",EDGE,"E12"),sQuery(id+"F0.wireOp",EDGE,"E14.0.MirrorC"),sQuery(id+"F0.wireOp",EDGE,"E16.0.MirrorCS"),sQuery(id+"F0.wireOp",EDGE,"E16.1.MirrorCS"),sQuery(id+"F0.wireOp",EDGE,"E16.3.MirrorCS"),sQuery(id+"F0.wireOp",EDGE,"E16.8.MirrorCS"),sQuery(id+"F0.wireOp",EDGE,"E16.11.MirrorCS"),sQuery(id+"F0.wireOp",EDGE,"E17"),sQuery(id+"F0.wireOp",EDGE,"E18.1.MirrorCS"),sQuery(id+"F0.wireOp",EDGE,"E18.2.MirrorCS"),sQuery(id+"F0.wireOp",EDGE,"E18.5.MirrorCS"),sQuery(id+"F0.wireOp",EDGE,"E18.6.MirrorCS"),sQuery(id+"F0.wireOp",EDGE,"E18.7.MirrorCS"),sQuery(id+"F0.wireOp",EDGE,"E18.10.MirrorCS"),sQuery(id+"F0.wireOp",EDGE,"E18.11.MirrorCS"),sQuery(id+"F0.wireOp",EDGE,"E18.14.MirrorCS"),sQuery(id+"F0.wireOp",EDGE,"E18.15.MirrorCS"),sQuery(id+"F0.wireOp",EDGE,"E18.17.MirrorCS"),sQuery(id+"F0.wireOp",EDGE,"E18.18.MirrorCS"),sQuery(id+"F0.wireOp",EDGE,"E18.20.MirrorCS"),sQuery(id+"F0.wireOp",EDGE,"E18.21.MirrorCS"),sQuery(id+"F0.wireOp",EDGE,"E18.24.MirrorCS"),sQuery(id+"F0.wireOp",EDGE,"E18.25.MirrorCS"),sQuery(id+"F0.wireOp",EDGE,"E18.26.MirrorCS"),sQuery(id+"F0.wireOp",EDGE,"E18.3.MirrorCS"),sQuery(id+"F0.wireOp",EDGE,"E19"),sQuery(id+"F0.wireOp",EDGE,"E21"),sQuery(id+"F0.wireOp",EDGE,"E23.0.MirrorCS"),sQuery(id+"F0.wireOp",EDGE,"E26.0.MirrorCS"),sQuery(id+"F0.wireOp",EDGE,"E27.0.MirrorCS"),sQuery(id+"F0.wireOp",EDGE,"E28.0.MirrorCS"),sQuery(id+"F0.wireOp",EDGE,"E29.0.MirrorCS"),sQuery(id+"F0.wireOp",EDGE,"E30.0.MirrorCS"),sQuery(id+"F0.wireOp",EDGE,"E31.0.MirrorCS"),sQuery(id+"F0.wireOp",EDGE,"E32.0.MirrorCS"),sQuery(id+"F0.wireOp",EDGE,"E33.0.MirrorCS"),sQuery(id+"F0.wireOp",EDGE,"E34.0.MirrorCS"),sQuery(id+"F0.wireOp",EDGE,"E35.0.MirrorCS"),sQuery(id+"F0.wireOp",EDGE,"E37.filletArc"),sQuery(id+"F0.wireOp",EDGE,"E38.filletArc"),sQuery(id+"F0.wireOp",EDGE,"E39.filletArc"),sQuery(id+"F0.wireOp",EDGE,"E40.filletArc"),sQuery(id+"F0.wireOp",EDGE,"E41.1.MirrorCS"),sQuery(id+"F0.wireOp",EDGE,"E41.5.MirrorCS"),sQuery(id+"F0.wireOp",EDGE,"E41.12.MirrorCS"),sQuery(id+"F0.wireOp",EDGE,"E41.15.MirrorCS"),sQuery(id+"F0.wireOp",EDGE,"E41.24.MirrorCS"),sQuery(id+"F0.wireOp",EDGE,"E42.1.MirrorCS"),sQuery(id+"F0.wireOp",EDGE,"E42.3.MirrorCS"),sQuery(id+"F0.wireOp",EDGE,"E42.10.MirrorCS"),sQuery(id+"F0.wireOp",EDGE,"E42.22.MirrorCS"),sQuery(id+"F0.wireOp",EDGE,"E42.25.MirrorCS"),sQuery(id+"F0.wireOp",EDGE,"E42.30.MirrorCS"),sQuery(id+"F0.wireOp",EDGE,"E43.filletArc"),sQuery(id+"F0.wireOp",EDGE,"E44.filletArc"),sQuery(id+"F0.wireOp",EDGE,"E45"),sQuery(id+"F0.wireOp",EDGE,"E46"),sQuery(id+"F0.wireOp",EDGE,"E47.0"),sQuery(id+"F0.wireOp",EDGE,"E48.0"),sQuery(id+"F0.wireOp",EDGE,"E49.filletArc"),sQuery(id+"F0.wireOp",EDGE,"E50.filletArc"),sQuery(id+"F0.wireOp",EDGE,"E51.0.MirrorCS"),sQuery(id+"F0.wireOp",EDGE,"E52.0.MirrorCS"),sQuery(id+"F0.wireOp",EDGE,"E53.0.MirrorCS"),sQuery(id+"F0.wireOp",EDGE,"E55.filletArc"),sQuery(id+"F0.wireOp",EDGE,"E56.0.MirrorCS"),sQuery(id+"F0.wireOp",EDGE,"E57.0.MirrorCS"),sQuery(id+"F0.wireOp",EDGE,"E58.0.MirrorCS"),sQuery(id+"F0.wireOp",EDGE,"E62.0.MirrorCS"),sQuery(id+"F0.wireOp",EDGE,"E63.0.MirrorCS"),sQuery(id+"F0.wireOp",EDGE,"E64.0.MirrorCS"),sQuery(id+"F0.wireOp",EDGE,"E65.0.MirrorCS"),sQuery(id+"F0.wireOp",EDGE,"E66.0.MirrorCS"),sQuery(id+"F0.wireOp",EDGE,"E67.0.MirrorCS"),sQuery(id+"F0.wireOp",EDGE,"E69.0.MirrorCS"),sQuery(id+"F0.wireOp",EDGE,"E68.0.MirrorCS"),sQuery(id+"F0.wireOp",EDGE,"E70.0.MirrorCS"),sQuery(id+"F0.wireOp",EDGE,"E71.0.MirrorCS"),sQuery(id+"F0.wireOp",EDGE,"E72.0.MirrorCS"),sQuery(id+"F0.wireOp",EDGE,"E73.0.MirrorCS"),sQuery(id+"F0.wireOp",EDGE,"E74.0.MirrorCS"),sQuery(id+"F0.wireOp",EDGE,"E76.0.MirrorCS"),sQuery(id+"F0.wireOp",EDGE,"E76.1.MirrorCS"),sQuery(id+"F0.wireOp",EDGE,"E76.2.MirrorCS"),sQuery(id+"F0.wireOp",EDGE,"E76.3.MirrorCS"),sQuery(id+"F0.wireOp",EDGE,"E77.0.MirrorCS"),sQuery(id+"F0.wireOp",EDGE,"E78.0.MirrorCS"),sQuery(id+"F0.wireOp",EDGE,"E79.0.MirrorCS"),sQuery(id+"F0.wireOp",EDGE,"E80.0.MirrorCS"),sQuery(id+"F0.wireOp",EDGE,"E81.0.MirrorCS"),sQuery(id+"F0.wireOp",EDGE,"E82.0.MirrorCS"),sQuery(id+"F0.wireOp",EDGE,"E83.0.MirrorCS"),sQuery(id+"F0.wireOp",EDGE,"E84.0.MirrorCS"),sQuery(id+"F0.wireOp",EDGE,"E85.0.MirrorCS"),sQuery(id+"F0.wireOp",EDGE,"E86.0.MirrorCS"),sQuery(id+"F0.wireOp",EDGE,"E87.2.MirrorCS"),sQuery(id+"F0.wireOp",EDGE,"E87.4.MirrorCS"),sQuery(id+"F0.wireOp",EDGE,"E87.6.MirrorCS"),sQuery(id+"F0.wireOp",EDGE,"E87.8.MirrorCS"),sQuery(id+"F0.wireOp",EDGE,"E87.10.MirrorCS"),sQuery(id+"F0.wireOp",EDGE,"E87.15.MirrorCS"),sQuery(id+"F0.wireOp",EDGE,"E87.19.MirrorCS"),sQuery(id+"F0.wireOp",EDGE,"E87.20.MirrorCS"),sQuery(id+"F0.wireOp",EDGE,"E87.24.MirrorCS"),sQuery(id+"F0.wireOp",EDGE,"E87.25.MirrorCS"),sQuery(id+"F0.wireOp",EDGE,"E87.26.MirrorCS"),sQuery(id+"F0.wireOp",EDGE,"E87.28.MirrorCS"),sQuery(id+"F0.wireOp",EDGE,"E87.31.MirrorCS"),sQuery(id+"F0.wireOp",EDGE,"E87.35.MirrorCS"),sQuery(id+"F0.wireOp",EDGE,"E87.37.MirrorCS"),sQuery(id+"F0.wireOp",EDGE,"E87.38.MirrorCS"),sQuery(id+"F0.wireOp",EDGE,"E87.44.MirrorCS"),sQuery(id+"F0.wireOp",EDGE,"E41.30.MirrorCS"),sQuery(id+"F0.wireOp",EDGE,"E87.52.MirrorCS"),sQuery(id+"F0.wireOp",EDGE,"E87.55.MirrorCS"),sQuery(id+"F0.wireOp",EDGE,"E41.10.MirrorC"),sQuery(id+"F0.wireOp",EDGE,"E87.57.MirrorCS"),sQuery(id+"F0.wireOp",EDGE,"E87.61.MirrorCS"),sQuery(id+"F0.wireOp",EDGE,"E87.65.MirrorCS"),sQuery(id+"F0.wireOp",EDGE,"E87.70.MirrorCS"),sQuery(id+"F0.wireOp",EDGE,"E42.27.MirrorC"),sQuery(id+"F0.wireOp",EDGE,"E88.0.MirrorCS"),sQuery(id+"F0.wireOp",EDGE,"E89.0.MirrorCS"),sQuery(id+"F0.wireOp",EDGE,"E90.0.MirrorCS"),sQuery(id+"F0.wireOp",EDGE,"E91.0.MirrorCS"),sQuery(id+"F0.wireOp",EDGE,"E92.0.MirrorCS"),sQuery(id+"F0.wireOp",EDGE,"E93.0.MirrorCS"),sQuery(id+"F0.wireOp",EDGE,"E94.0.MirrorCS"),sQuery(id+"F0.wireOp",EDGE,"E95.filletArc"),sQuery(id+"F0.wireOp",EDGE,"E96.filletArc"),sQuery(id+"F0.wireOp",EDGE,"E97.0.MirrorCS"),sQuery(id+"F0.wireOp",EDGE,"E98.filletArc"),sQuery(id+"F0.wireOp",EDGE,"E99.filletArc"),sQuery(id+"F0.wireOp",EDGE,"E104"),sQuery(id+"F0.wireOp",EDGE,"E105.filletArc"),sQuery(id+"F0.wireOp",EDGE,"E54.0.MirrorCS"),sQuery(id+"F0.wireOp",EDGE,"E107"),sQuery(id+"F0.wireOp",EDGE,"E110.filletArc"),sQuery(id+"F0.wireOp",EDGE,"E111.filletArc"),sQuery(id+"F0.wireOp",EDGE,"E112.0.MirrorCS"),sQuery(id+"F0.wireOp",EDGE,"E113.0.MirrorCS"),sQuery(id+"F0.wireOp",EDGE,"E114.0.MirrorCS"),sQuery(id+"F0.wireOp",EDGE,"E117.filletArc"),sQuery(id+"F0.wireOp",EDGE,"E118.filletArc"),sQuery(id+"F0.wireOp",EDGE,"E122.filletArc"),sQuery(id+"F0.wireOp",EDGE,"E124")])]});
            transform(context, id + "F3", {"entities" : qUnion([Q0]), "transformType" : TransformType.TRANSLATION_3D, "dx" : 0 * mm, "dy" : 0 * mm, "dz" : 0 * mm, "makeCopy" : true});
        }
        {
            var Q0;
            Q0=makeQuery(id+"F3.opPattern","COPY",BODY,{"derivedFrom":makeQuery(id+"F1.opExtrude","SWEPT_BODY",BODY,{"disambiguationData":[OSD([sQuery(id+"F0.wireOp",EDGE,"E1"),sQuery(id+"F0.wireOp",EDGE,"E2"),sQuery(id+"F0.wireOp",EDGE,"E3"),sQuery(id+"F0.wireOp",EDGE,"E4"),sQuery(id+"F0.wireOp",EDGE,"E5"),sQuery(id+"F0.wireOp",EDGE,"E6"),sQuery(id+"F0.wireOp",EDGE,"E7"),sQuery(id+"F0.wireOp",EDGE,"E9.filletArc"),sQuery(id+"F0.wireOp",EDGE,"E10.filletArc"),sQuery(id+"F0.wireOp",EDGE,"E11.filletArc"),sQuery(id+"F0.wireOp",EDGE,"E12"),sQuery(id+"F0.wireOp",EDGE,"E14.0.MirrorC"),sQuery(id+"F0.wireOp",EDGE,"E16.0.MirrorCS"),sQuery(id+"F0.wireOp",EDGE,"E16.1.MirrorCS"),sQuery(id+"F0.wireOp",EDGE,"E16.3.MirrorCS"),sQuery(id+"F0.wireOp",EDGE,"E16.8.MirrorCS"),sQuery(id+"F0.wireOp",EDGE,"E16.11.MirrorCS"),sQuery(id+"F0.wireOp",EDGE,"E17"),sQuery(id+"F0.wireOp",EDGE,"E18.1.MirrorCS"),sQuery(id+"F0.wireOp",EDGE,"E18.2.MirrorCS"),sQuery(id+"F0.wireOp",EDGE,"E18.5.MirrorCS"),sQuery(id+"F0.wireOp",EDGE,"E18.6.MirrorCS"),sQuery(id+"F0.wireOp",EDGE,"E18.7.MirrorCS"),sQuery(id+"F0.wireOp",EDGE,"E18.10.MirrorCS"),sQuery(id+"F0.wireOp",EDGE,"E18.11.MirrorCS"),sQuery(id+"F0.wireOp",EDGE,"E18.14.MirrorCS"),sQuery(id+"F0.wireOp",EDGE,"E18.15.MirrorCS"),sQuery(id+"F0.wireOp",EDGE,"E18.17.MirrorCS"),sQuery(id+"F0.wireOp",EDGE,"E18.18.MirrorCS"),sQuery(id+"F0.wireOp",EDGE,"E18.20.MirrorCS"),sQuery(id+"F0.wireOp",EDGE,"E18.21.MirrorCS"),sQuery(id+"F0.wireOp",EDGE,"E18.24.MirrorCS"),sQuery(id+"F0.wireOp",EDGE,"E18.25.MirrorCS"),sQuery(id+"F0.wireOp",EDGE,"E18.26.MirrorCS"),sQuery(id+"F0.wireOp",EDGE,"E18.3.MirrorCS"),sQuery(id+"F0.wireOp",EDGE,"E19"),sQuery(id+"F0.wireOp",EDGE,"E21"),sQuery(id+"F0.wireOp",EDGE,"E23.0.MirrorCS"),sQuery(id+"F0.wireOp",EDGE,"E26.0.MirrorCS"),sQuery(id+"F0.wireOp",EDGE,"E27.0.MirrorCS"),sQuery(id+"F0.wireOp",EDGE,"E28.0.MirrorCS"),sQuery(id+"F0.wireOp",EDGE,"E29.0.MirrorCS"),sQuery(id+"F0.wireOp",EDGE,"E30.0.MirrorCS"),sQuery(id+"F0.wireOp",EDGE,"E31.0.MirrorCS"),sQuery(id+"F0.wireOp",EDGE,"E32.0.MirrorCS"),sQuery(id+"F0.wireOp",EDGE,"E33.0.MirrorCS"),sQuery(id+"F0.wireOp",EDGE,"E34.0.MirrorCS"),sQuery(id+"F0.wireOp",EDGE,"E35.0.MirrorCS"),sQuery(id+"F0.wireOp",EDGE,"E37.filletArc"),sQuery(id+"F0.wireOp",EDGE,"E38.filletArc"),sQuery(id+"F0.wireOp",EDGE,"E39.filletArc"),sQuery(id+"F0.wireOp",EDGE,"E40.filletArc"),sQuery(id+"F0.wireOp",EDGE,"E41.1.MirrorCS"),sQuery(id+"F0.wireOp",EDGE,"E41.5.MirrorCS"),sQuery(id+"F0.wireOp",EDGE,"E41.12.MirrorCS"),sQuery(id+"F0.wireOp",EDGE,"E41.15.MirrorCS"),sQuery(id+"F0.wireOp",EDGE,"E41.24.MirrorCS"),sQuery(id+"F0.wireOp",EDGE,"E42.1.MirrorCS"),sQuery(id+"F0.wireOp",EDGE,"E42.3.MirrorCS"),sQuery(id+"F0.wireOp",EDGE,"E42.10.MirrorCS"),sQuery(id+"F0.wireOp",EDGE,"E42.22.MirrorCS"),sQuery(id+"F0.wireOp",EDGE,"E42.25.MirrorCS"),sQuery(id+"F0.wireOp",EDGE,"E42.30.MirrorCS"),sQuery(id+"F0.wireOp",EDGE,"E43.filletArc"),sQuery(id+"F0.wireOp",EDGE,"E44.filletArc"),sQuery(id+"F0.wireOp",EDGE,"E45"),sQuery(id+"F0.wireOp",EDGE,"E46"),sQuery(id+"F0.wireOp",EDGE,"E47.0"),sQuery(id+"F0.wireOp",EDGE,"E48.0"),sQuery(id+"F0.wireOp",EDGE,"E49.filletArc"),sQuery(id+"F0.wireOp",EDGE,"E50.filletArc"),sQuery(id+"F0.wireOp",EDGE,"E51.0.MirrorCS"),sQuery(id+"F0.wireOp",EDGE,"E52.0.MirrorCS"),sQuery(id+"F0.wireOp",EDGE,"E53.0.MirrorCS"),sQuery(id+"F0.wireOp",EDGE,"E55.filletArc"),sQuery(id+"F0.wireOp",EDGE,"E56.0.MirrorCS"),sQuery(id+"F0.wireOp",EDGE,"E57.0.MirrorCS"),sQuery(id+"F0.wireOp",EDGE,"E58.0.MirrorCS"),sQuery(id+"F0.wireOp",EDGE,"E62.0.MirrorCS"),sQuery(id+"F0.wireOp",EDGE,"E63.0.MirrorCS"),sQuery(id+"F0.wireOp",EDGE,"E64.0.MirrorCS"),sQuery(id+"F0.wireOp",EDGE,"E65.0.MirrorCS"),sQuery(id+"F0.wireOp",EDGE,"E66.0.MirrorCS"),sQuery(id+"F0.wireOp",EDGE,"E67.0.MirrorCS"),sQuery(id+"F0.wireOp",EDGE,"E69.0.MirrorCS"),sQuery(id+"F0.wireOp",EDGE,"E68.0.MirrorCS"),sQuery(id+"F0.wireOp",EDGE,"E70.0.MirrorCS"),sQuery(id+"F0.wireOp",EDGE,"E71.0.MirrorCS"),sQuery(id+"F0.wireOp",EDGE,"E72.0.MirrorCS"),sQuery(id+"F0.wireOp",EDGE,"E73.0.MirrorCS"),sQuery(id+"F0.wireOp",EDGE,"E74.0.MirrorCS"),sQuery(id+"F0.wireOp",EDGE,"E76.0.MirrorCS"),sQuery(id+"F0.wireOp",EDGE,"E76.1.MirrorCS"),sQuery(id+"F0.wireOp",EDGE,"E76.2.MirrorCS"),sQuery(id+"F0.wireOp",EDGE,"E76.3.MirrorCS"),sQuery(id+"F0.wireOp",EDGE,"E77.0.MirrorCS"),sQuery(id+"F0.wireOp",EDGE,"E78.0.MirrorCS"),sQuery(id+"F0.wireOp",EDGE,"E79.0.MirrorCS"),sQuery(id+"F0.wireOp",EDGE,"E80.0.MirrorCS"),sQuery(id+"F0.wireOp",EDGE,"E81.0.MirrorCS"),sQuery(id+"F0.wireOp",EDGE,"E82.0.MirrorCS"),sQuery(id+"F0.wireOp",EDGE,"E83.0.MirrorCS"),sQuery(id+"F0.wireOp",EDGE,"E84.0.MirrorCS"),sQuery(id+"F0.wireOp",EDGE,"E85.0.MirrorCS"),sQuery(id+"F0.wireOp",EDGE,"E86.0.MirrorCS"),sQuery(id+"F0.wireOp",EDGE,"E87.2.MirrorCS"),sQuery(id+"F0.wireOp",EDGE,"E87.4.MirrorCS"),sQuery(id+"F0.wireOp",EDGE,"E87.6.MirrorCS"),sQuery(id+"F0.wireOp",EDGE,"E87.8.MirrorCS"),sQuery(id+"F0.wireOp",EDGE,"E87.10.MirrorCS"),sQuery(id+"F0.wireOp",EDGE,"E87.15.MirrorCS"),sQuery(id+"F0.wireOp",EDGE,"E87.19.MirrorCS"),sQuery(id+"F0.wireOp",EDGE,"E87.20.MirrorCS"),sQuery(id+"F0.wireOp",EDGE,"E87.24.MirrorCS"),sQuery(id+"F0.wireOp",EDGE,"E87.25.MirrorCS"),sQuery(id+"F0.wireOp",EDGE,"E87.26.MirrorCS"),sQuery(id+"F0.wireOp",EDGE,"E87.28.MirrorCS"),sQuery(id+"F0.wireOp",EDGE,"E87.31.MirrorCS"),sQuery(id+"F0.wireOp",EDGE,"E87.35.MirrorCS"),sQuery(id+"F0.wireOp",EDGE,"E87.37.MirrorCS"),sQuery(id+"F0.wireOp",EDGE,"E87.38.MirrorCS"),sQuery(id+"F0.wireOp",EDGE,"E87.44.MirrorCS"),sQuery(id+"F0.wireOp",EDGE,"E41.30.MirrorCS"),sQuery(id+"F0.wireOp",EDGE,"E87.52.MirrorCS"),sQuery(id+"F0.wireOp",EDGE,"E87.55.MirrorCS"),sQuery(id+"F0.wireOp",EDGE,"E41.10.MirrorC"),sQuery(id+"F0.wireOp",EDGE,"E87.57.MirrorCS"),sQuery(id+"F0.wireOp",EDGE,"E87.61.MirrorCS"),sQuery(id+"F0.wireOp",EDGE,"E87.65.MirrorCS"),sQuery(id+"F0.wireOp",EDGE,"E87.70.MirrorCS"),sQuery(id+"F0.wireOp",EDGE,"E42.27.MirrorC"),sQuery(id+"F0.wireOp",EDGE,"E88.0.MirrorCS"),sQuery(id+"F0.wireOp",EDGE,"E89.0.MirrorCS"),sQuery(id+"F0.wireOp",EDGE,"E90.0.MirrorCS"),sQuery(id+"F0.wireOp",EDGE,"E91.0.MirrorCS"),sQuery(id+"F0.wireOp",EDGE,"E92.0.MirrorCS"),sQuery(id+"F0.wireOp",EDGE,"E93.0.MirrorCS"),sQuery(id+"F0.wireOp",EDGE,"E94.0.MirrorCS"),sQuery(id+"F0.wireOp",EDGE,"E95.filletArc"),sQuery(id+"F0.wireOp",EDGE,"E96.filletArc"),sQuery(id+"F0.wireOp",EDGE,"E97.0.MirrorCS"),sQuery(id+"F0.wireOp",EDGE,"E98.filletArc"),sQuery(id+"F0.wireOp",EDGE,"E99.filletArc"),sQuery(id+"F0.wireOp",EDGE,"E104"),sQuery(id+"F0.wireOp",EDGE,"E105.filletArc"),sQuery(id+"F0.wireOp",EDGE,"E54.0.MirrorCS"),sQuery(id+"F0.wireOp",EDGE,"E107"),sQuery(id+"F0.wireOp",EDGE,"E110.filletArc"),sQuery(id+"F0.wireOp",EDGE,"E111.filletArc"),sQuery(id+"F0.wireOp",EDGE,"E112.0.MirrorCS"),sQuery(id+"F0.wireOp",EDGE,"E113.0.MirrorCS"),sQuery(id+"F0.wireOp",EDGE,"E114.0.MirrorCS"),sQuery(id+"F0.wireOp",EDGE,"E117.filletArc"),sQuery(id+"F0.wireOp",EDGE,"E118.filletArc"),sQuery(id+"F0.wireOp",EDGE,"E122.filletArc"),sQuery(id+"F0.wireOp",EDGE,"E124")])]}),"instanceName":"1"});
            transform(context, id + "F4", {"entities" : qUnion([Q0]), "transformType" : TransformType.TRANSLATION_3D, "dx" : 0 * mm, "dy" : 0 * mm, "dz" : 0 * mm, "makeCopy" : true});
        }
    });
